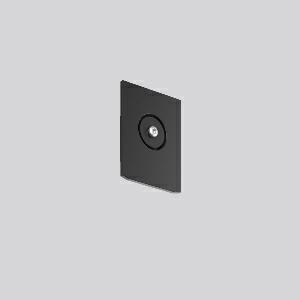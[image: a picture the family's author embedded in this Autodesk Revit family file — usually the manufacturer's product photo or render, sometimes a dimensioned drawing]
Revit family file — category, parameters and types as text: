
# Revit family: linedo_endkappe_s_f_982699_003_e9aa
name_source: partatom
category: Lighting Fixtures
units: mm (PartAtom-declared; Revit-internal decimal feet)

## family parameters
Cut with Voids When Loaded = No
Host = Face
Light Source = No
Part Type = Normal
Room Calculation Point = No
Round Connector Dimension = Use Diameter
Shared = No

## types (1)
- LINEDO_Endkappe_S_F
    Apparent Load = 0 VA
    Default Elevation = 1800 mm
    Description = End cap low profile for LINEDO socket. Plastic end cap to cover the LINEDO plug system at the end of the line. Fastening by TX20 screw. Installation accessories included.
Colour: black
Length: 16 mm
Width: 58 mm
Height: 76 mm
Weight: 21,5 g
    Height = 76 mm
    Lamp = 0 x
    Length = 17 mm
    Luminous efficacy = 0 lm/W
    Manufacturer = RZB
    ModVariant = No
    Model = 982699.003
    Mounting Place = Ceiling
    Mounting Type = Surface mounted, Pendant
    Number of Poles = 1
    OnlyDefault = Yes
    Power Factor = 1
    Product Name = LINEDO_Endkappe_S_F
    Product group = Surface mounted continuous line luminaire system
    ProductGroupID = 310
    Protection Class = Protection class
    Protection Degree = Degree of protection
    RLX_Detail_Level = 1
    RLX_Emergency_Light_Flux = 0 lm
    RLX_Emergency_Type = 0
    RLX_Emergency_Type_DB = No
    RlxData = <blob elided: 9341 chars, md5=f27c35c5>
    Standby Power = 0 W
    System Light Flux = 0 lm
    System Power = 0 W
    Type Comments = Product without accessories
    Type Image = 982699.003.jpg
    URL = http://relux.com
    VarID = ---
    Voltage = 0 V
    Weight = 0.00 kg
    Width = 58 mm

## geometry (parser evidence)
native form markers: Sweep x9
no freeform markers — native parametric forms only
